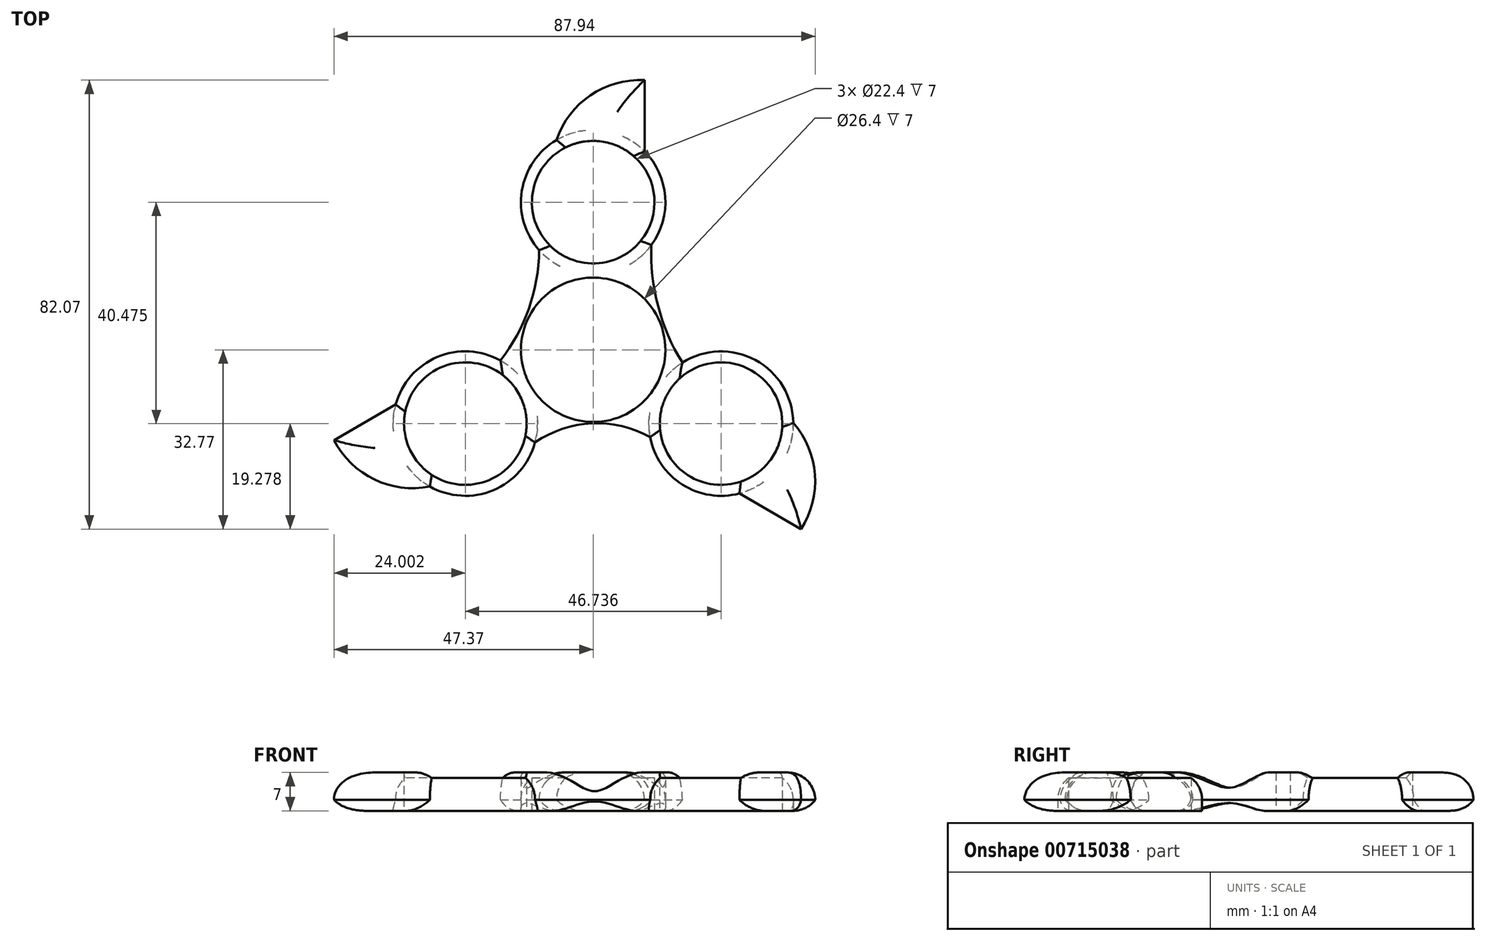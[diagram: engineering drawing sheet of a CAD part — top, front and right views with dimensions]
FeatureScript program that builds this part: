
annotation { "Feature Type Name" : "Feature", "Feature Type Description" : "" }
export const myFeature = defineFeature(function(context is Context, id is Id, definition is map)
    precondition{}
    {
        {
            var Q0;
            Q0=qCreatedBy(makeId("Top.planeOp"),FACE);
            var sketch = newSketch(context, id + "F0", { "sketchPlane" : qUnion([Q0])});
            skCircle(sketch, "E0", {"center": v(0, 0) * mm, "radius": 11.2 * mm});
            skCircle(sketch, "E1", {"center": v(0, 0) * mm, "radius": 13.2 * mm});
            skCircle(sketch, "E2", {"center": v(0, 26.98) * mm, "radius": 11.2 * mm});
            skCircle(sketch, "E3", {"center": v(0, 26.98) * mm, "radius": 13.2 * mm});
            skCircle(sketch, "E4.1.0", {"center": v(-23.37, -13.5) * mm, "radius": 13.2 * mm});
            skCircle(sketch, "E4.1.1", {"center": v(-23.37, -13.5) * mm, "radius": 11.2 * mm});
            skCircle(sketch, "E4.2.0", {"center": v(23.37, -13.5) * mm, "radius": 13.2 * mm});
            skCircle(sketch, "E4.2.1", {"center": v(23.37, -13.5) * mm, "radius": 11.2 * mm});
            skArc(sketch, "E5", {"start": v(-16.95, -1.96) * mm, "mid": v(-11.75, 7.54) * mm, "end": v(-9.87, 18.21) * mm});
            skArc(sketch, "E6", {"start": v(10.64, 19.17) * mm, "mid": v(11.86, 8) * mm, "end": v(16.3, -2.34) * mm});
            skArc(sketch, "E7", {"start": v(10.4, -15.95) * mm, "mid": v(-0.25, -13.45) * mm, "end": v(-10.63, -16.94) * mm});
            skArc(sketch, "E8", {"start": v(9.38, 49.28) * mm, "mid": v(-0.5, 46.5) * mm, "end": v(-6.72, 38.35) * mm});
            skLineSegment(sketch, "E9", {"start": v(9.38, 49.28) * mm, "end": v(9.38, 36.27) * mm});
            skArc(sketch, "E10.1.0", {"start": v(-47.37, -16.52) * mm, "mid": v(-40.03, -23.69) * mm, "end": v(-29.85, -24.99) * mm});
            skLineSegment(sketch, "E10.1.1", {"start": v(-47.37, -16.52) * mm, "end": v(-36.1, -10.01) * mm});
            skArc(sketch, "E10.2.0", {"start": v(38, -32.77) * mm, "mid": v(40.53, -22.82) * mm, "end": v(36.57, -13.36) * mm});
            skLineSegment(sketch, "E10.2.1", {"start": v(38, -32.77) * mm, "end": v(26.72, -26.26) * mm});
            skSolve(sketch);
        }
        {
            var Q0;
            Q0 = qSketchRegion(id + "F0", true);
            extrude(context, id + "F1", {"entities" : qUnion([Q0]), "depth" : 7 * mm, "offsetDistance" : 25 * mm});
        }
        {
            var Q0;
            Q0=makeQuery(id+"F1.opExtrude","CAP_EDGE",EDGE,{"disambiguationData":[OSD([sQuery(id+"F0.wireOp",EDGE,"E8")])],"isStart":false});
            var Q1;
            Q1=makeQuery(id+"F1.opExtrude","CAP_EDGE",EDGE,{"disambiguationData":[OSD([sQuery(id+"F0.wireOp",EDGE,"E9")])],"isStart":false});
            var Q2;
            {var subQ0=sQuery(id+"F0.wireOp",EDGE,"E3");Q2=makeQuery(id+"F1.opExtrude","CAP_EDGE",EDGE,{"disambiguationData":[OSD([subQ0]),TDD([makeQuery(id+"F0.imprint","IMPRINT",EDGE,{"disambiguationData":[TD([[makeQuery(id+"F0.imprint","INTERSECT",VERTEX,{"derivedFrom":[subQ0,sQuery(id+"F0.wireOp",EDGE,"E6")]}),-1.0]])],"derivedFrom":subQ0})])],"isStart":false});}
            var Q3;
            Q3=makeQuery(id+"F1.opExtrude","CAP_EDGE",EDGE,{"disambiguationData":[OSD([sQuery(id+"F0.wireOp",EDGE,"E6")])],"isStart":false});
            var Q4;
            {var subQ0=sQuery(id+"F0.wireOp",EDGE,"E4.2.0");Q4=makeQuery(id+"F1.opExtrude","CAP_EDGE",EDGE,{"disambiguationData":[OSD([subQ0]),TDD([makeQuery(id+"F0.imprint","IMPRINT",EDGE,{"disambiguationData":[TD([[makeQuery(id+"F0.imprint","INTERSECT",VERTEX,{"derivedFrom":[subQ0,sQuery(id+"F0.wireOp",EDGE,"E6")]}),1.0]])],"derivedFrom":subQ0})])],"isStart":false});}
            var Q5;
            Q5=makeQuery(id+"F1.opExtrude","CAP_EDGE",EDGE,{"disambiguationData":[OSD([sQuery(id+"F0.wireOp",EDGE,"E10.2.0")])],"isStart":false});
            var Q6;
            {var subQ0=sQuery(id+"F0.wireOp",EDGE,"E4.2.0");Q6=makeQuery(id+"F1.opExtrude","CAP_EDGE",EDGE,{"disambiguationData":[OSD([subQ0]),TDD([makeQuery(id+"F0.imprint","IMPRINT",EDGE,{"disambiguationData":[TD([[makeQuery(id+"F0.imprint","INTERSECT",VERTEX,{"derivedFrom":[subQ0,sQuery(id+"F0.wireOp",EDGE,"E7")]}),-1.0]])],"derivedFrom":subQ0})])],"isStart":false});}
            var Q7;
            Q7=makeQuery(id+"F1.opExtrude","CAP_EDGE",EDGE,{"disambiguationData":[OSD([sQuery(id+"F0.wireOp",EDGE,"E10.2.1")])],"isStart":false});
            var Q8;
            Q8=makeQuery(id+"F1.opExtrude","CAP_EDGE",EDGE,{"disambiguationData":[OSD([sQuery(id+"F0.wireOp",EDGE,"E7")])],"isStart":false});
            var Q9;
            {var subQ0=sQuery(id+"F0.wireOp",EDGE,"E4.1.0");Q9=makeQuery(id+"F1.opExtrude","CAP_EDGE",EDGE,{"disambiguationData":[OSD([subQ0]),TDD([makeQuery(id+"F0.imprint","IMPRINT",EDGE,{"disambiguationData":[TD([[makeQuery(id+"F0.imprint","INTERSECT",VERTEX,{"derivedFrom":[subQ0,sQuery(id+"F0.wireOp",EDGE,"E7")]}),1.0]])],"derivedFrom":subQ0})])],"isStart":false});}
            var Q10;
            Q10=makeQuery(id+"F1.opExtrude","CAP_EDGE",EDGE,{"disambiguationData":[OSD([sQuery(id+"F0.wireOp",EDGE,"E10.1.0")])],"isStart":false});
            var Q11;
            Q11=makeQuery(id+"F1.opExtrude","CAP_EDGE",EDGE,{"disambiguationData":[OSD([sQuery(id+"F0.wireOp",EDGE,"E10.1.1")])],"isStart":false});
            var Q12;
            {var subQ0=sQuery(id+"F0.wireOp",EDGE,"E4.1.0");Q12=makeQuery(id+"F1.opExtrude","CAP_EDGE",EDGE,{"disambiguationData":[OSD([subQ0]),TDD([makeQuery(id+"F0.imprint","IMPRINT",EDGE,{"disambiguationData":[TD([[makeQuery(id+"F0.imprint","INTERSECT",VERTEX,{"derivedFrom":[subQ0,sQuery(id+"F0.wireOp",EDGE,"E5")]}),-1.0]])],"derivedFrom":subQ0})])],"isStart":false});}
            var Q13;
            Q13=makeQuery(id+"F1.opExtrude","CAP_EDGE",EDGE,{"disambiguationData":[OSD([sQuery(id+"F0.wireOp",EDGE,"E5")])],"isStart":false});
            var Q14;
            {var subQ0=sQuery(id+"F0.wireOp",EDGE,"E3");Q14=makeQuery(id+"F1.opExtrude","CAP_EDGE",EDGE,{"disambiguationData":[OSD([subQ0]),TDD([makeQuery(id+"F0.imprint","IMPRINT",EDGE,{"disambiguationData":[TD([[makeQuery(id+"F0.imprint","INTERSECT",VERTEX,{"derivedFrom":[subQ0,sQuery(id+"F0.wireOp",EDGE,"E5")]}),1.0]])],"derivedFrom":subQ0})])],"isStart":false});}
            fillet(context, id + "F2", {"entities" : qUnion([Q0, Q1, Q2, Q3, Q4, Q5, Q6, Q7, Q8, Q9, Q10, Q11, Q12, Q13, Q14]), "radius" : 5 * mm, "tangentPropagation" : true, "allowEdgeOverflow" : false});
        }
        {
            var Q0;
            Q0=makeQuery(id+"F1.opExtrude","CAP_EDGE",EDGE,{"disambiguationData":[OSD([sQuery(id+"F0.wireOp",EDGE,"E9")])],"isStart":true});
            var Q1;
            Q1=makeQuery(id+"F1.opExtrude","CAP_EDGE",EDGE,{"disambiguationData":[OSD([sQuery(id+"F0.wireOp",EDGE,"E5")])],"isStart":true});
            var Q2;
            Q2=makeQuery(id+"F1.opExtrude","CAP_EDGE",EDGE,{"disambiguationData":[OSD([sQuery(id+"F0.wireOp",EDGE,"E6")])],"isStart":true});
            var Q3;
            Q3=makeQuery(id+"F1.opExtrude","CAP_EDGE",EDGE,{"disambiguationData":[OSD([sQuery(id+"F0.wireOp",EDGE,"E7")])],"isStart":true});
            var Q4;
            Q4=makeQuery(id+"F1.opExtrude","CAP_EDGE",EDGE,{"disambiguationData":[OSD([sQuery(id+"F0.wireOp",EDGE,"E8")])],"isStart":true});
            var Q5;
            Q5=makeQuery(id+"F1.opExtrude","CAP_EDGE",EDGE,{"disambiguationData":[OSD([sQuery(id+"F0.wireOp",EDGE,"E10.1.1")])],"isStart":true});
            var Q6;
            Q6=makeQuery(id+"F1.opExtrude","CAP_EDGE",EDGE,{"disambiguationData":[OSD([sQuery(id+"F0.wireOp",EDGE,"E10.1.0")])],"isStart":true});
            var Q7;
            Q7=makeQuery(id+"F1.opExtrude","CAP_EDGE",EDGE,{"disambiguationData":[OSD([sQuery(id+"F0.wireOp",EDGE,"E10.2.1")])],"isStart":true});
            var Q8;
            Q8=makeQuery(id+"F1.opExtrude","CAP_EDGE",EDGE,{"disambiguationData":[OSD([sQuery(id+"F0.wireOp",EDGE,"E10.2.0")])],"isStart":true});
            fillet(context, id + "F3", {"entities" : qUnion([Q0, Q1, Q2, Q3, Q4, Q5, Q6, Q7, Q8]), "radius" : 5 * mm, "tangentPropagation" : true, "allowEdgeOverflow" : false});
        }
    });
